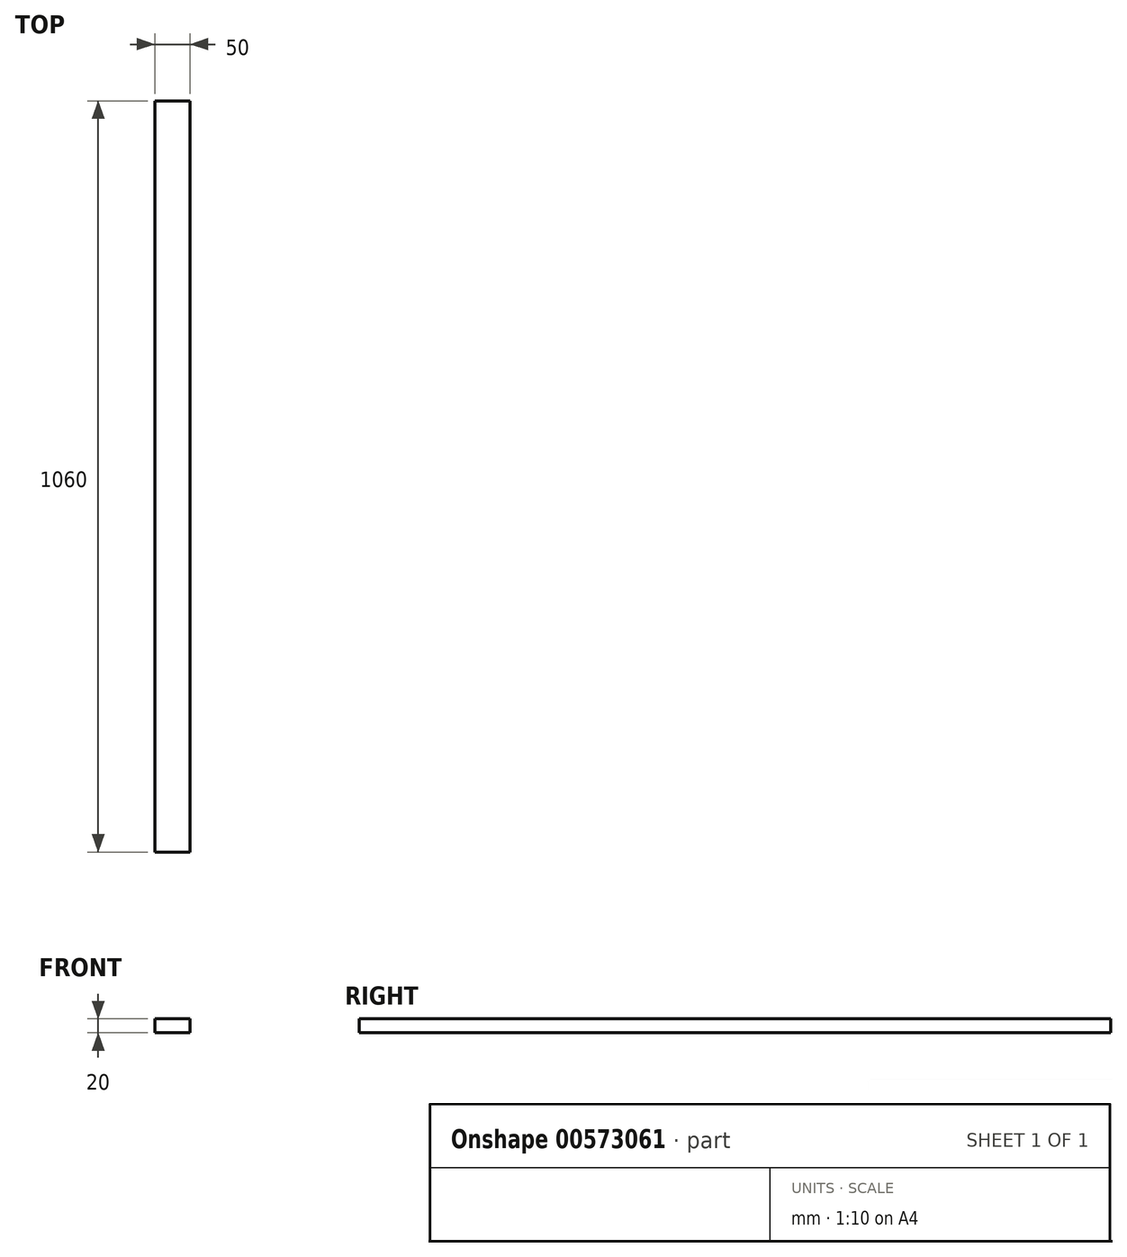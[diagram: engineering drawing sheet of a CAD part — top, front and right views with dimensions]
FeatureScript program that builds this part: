
annotation { "Feature Type Name" : "Feature", "Feature Type Description" : "" }
export const myFeature = defineFeature(function(context is Context, id is Id, definition is map)
    precondition{}
    {
        {
            var Q0;
            Q0=qCreatedBy(makeId("Front.planeOp"),FACE);
            var sketch = newSketch(context, id + "F0", { "sketchPlane" : qUnion([Q0])});
            skLineSegment(sketch, "E0.bottom", {"start": v(-92.53, 0) * mm, "end": v(-42.53, 0) * mm});
            skLineSegment(sketch, "E0.top", {"start": v(-92.53, -20) * mm, "end": v(-42.53, -20) * mm});
            skLineSegment(sketch, "E0.left", {"start": v(-92.53, 0) * mm, "end": v(-92.53, -20) * mm});
            skLineSegment(sketch, "E0.right", {"start": v(-42.53, 0) * mm, "end": v(-42.53, -20) * mm});
            skSolve(sketch);
        }
        {
            var Q0;
            Q0 = qSketchRegion(id + "F0", true);
            extrude(context, id + "F1", {"entities" : qUnion([Q0]), "depth" : 1060 * mm, "offsetDistance" : 25 * mm});
        }
    });
